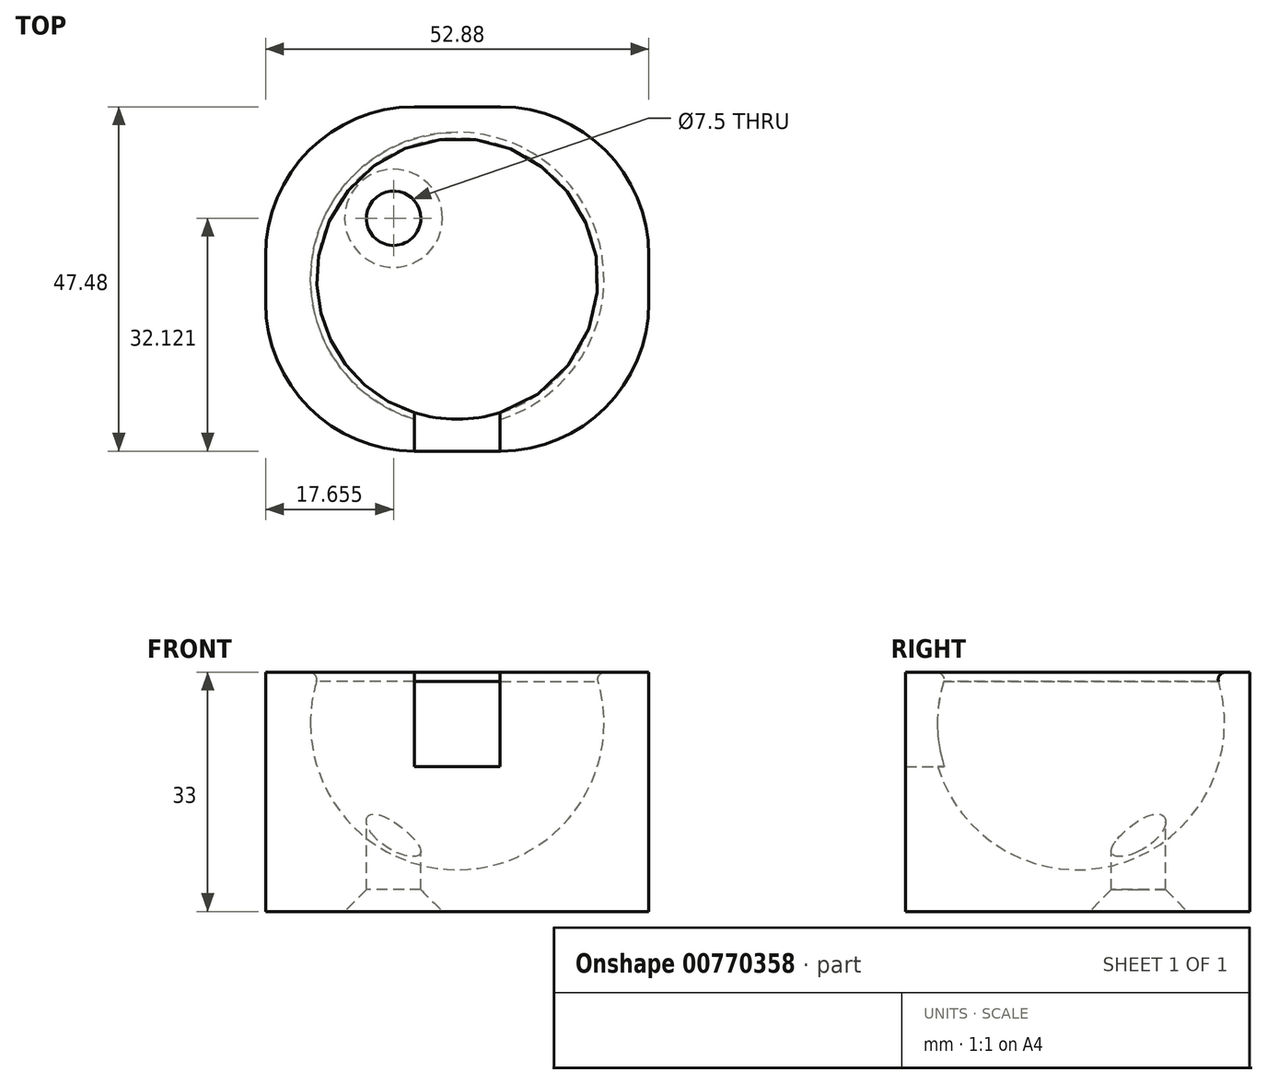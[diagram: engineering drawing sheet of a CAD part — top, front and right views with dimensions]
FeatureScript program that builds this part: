
annotation { "Feature Type Name" : "Feature", "Feature Type Description" : "" }
export const myFeature = defineFeature(function(context is Context, id is Id, definition is map)
    precondition{}
    {
        {
            var Q0;
            Q0=qCreatedBy(makeId("Top.planeOp"),FACE);
            var sketch = newSketch(context, id + "F0", { "sketchPlane" : qUnion([Q0])});
            skLineSegment(sketch, "E0", {"start": v(0, 20.25) * mm, "end": v(0, -20.25) * mm});
            skArc(sketch, "E1", {"start": v(0, 20.25) * mm, "mid": v(-20.25, 0) * mm, "end": v(0, -20.25) * mm});
            skSolve(sketch);
        }
        {
            var Q0;
            Q0=makeQuery(id+"F0.imprint","IMPRINT",FACE,{"disambiguationData":[TD([[makeQuery(id+"F0.imprint","IMPRINT",EDGE,{"derivedFrom":sQuery(id+"F0.wireOp",EDGE,"E0")}),-1.0]])]});
            var Q1;
            Q1=sQuery(id+"F0.wireOp",EDGE,"E0");
            revolve(context, id + "F1", {"surfaceOperationType" : NewSurfaceOperationType.NEW, "entities" : qUnion([Q0]), "axis" : qUnion([Q1]), "revolveType" : RevolveType.FULL});
        }
        {
            var Q0;
            Q0=qCreatedBy(makeId("Top.planeOp"),FACE);
            var sketch = newSketch(context, id + "F2", { "sketchPlane" : qUnion([Q0])});
            skLineSegment(sketch, "E2.bottom", {"start": v(26.44, -23.74) * mm, "end": v(-26.44, -23.74) * mm});
            skLineSegment(sketch, "E2.top", {"start": v(26.44, 23.74) * mm, "end": v(-26.44, 23.74) * mm});
            skLineSegment(sketch, "E2.left", {"start": v(26.44, -23.74) * mm, "end": v(26.44, 23.74) * mm});
            skLineSegment(sketch, "E2.right", {"start": v(-26.44, -23.74) * mm, "end": v(-26.44, 23.74) * mm});
            skPoint(sketch, "E2.middle", {"position": v(0, 0) * mm});
            skSolve(sketch);
        }
        {
            var Q0;
            Q0=makeQuery(id+"F2.imprint","IMPRINT",FACE,{"disambiguationData":[TD([[makeQuery(id+"F2.imprint","IMPRINT",EDGE,{"derivedFrom":sQuery(id+"F2.wireOp",EDGE,"E2.bottom")}),-1.0]])]});
            extrude(context, id + "F3", {"entities" : qUnion([Q0]), "endBound" : BoundingType.SYMMETRIC, "depth" : 52 * mm, "offsetDistance" : 25 * mm});
        }
        {
            var Q0;
            Q0=makeQuery(id+"F1.opRevolve","SWEPT_BODY",BODY,{"disambiguationData":[OSD([sQuery(id+"F0.wireOp",EDGE,"E0"),sQuery(id+"F0.wireOp",EDGE,"E1")])]});
            var Q1;
            Q1=makeQuery(id+"F3.opExtrude","SWEPT_BODY",BODY,{"disambiguationData":[OSD([sQuery(id+"F2.wireOp",EDGE,"E2.bottom"),sQuery(id+"F2.wireOp",EDGE,"E2.top"),sQuery(id+"F2.wireOp",EDGE,"E2.left"),sQuery(id+"F2.wireOp",EDGE,"E2.right")])]});
            booleanBodies(context, id + "F4", {"operationType" : BooleanOperationType.SUBTRACTION, "tools" : qUnion([Q0]), "targets" : qUnion([Q1])});
        }
        {
            var Q0;
            Q0=makeQuery(id+"F3.opExtrude","CAP_FACE",FACE,{"disambiguationData":[OSD([sQuery(id+"F2.wireOp",EDGE,"E2.bottom"),sQuery(id+"F2.wireOp",EDGE,"E2.top"),sQuery(id+"F2.wireOp",EDGE,"E2.left"),sQuery(id+"F2.wireOp",EDGE,"E2.right")])],"isStart":false});
            extrude(context, id + "F5", {"entities" : qUnion([Q0]), "operationType" : NewBodyOperationType.REMOVE, "oppositeDirection" : true, "depth" : 19 * mm, "offsetDistance" : 25 * mm});
        }
        {
            var Q0;
            Q0=qCreatedBy(makeId("Top.planeOp"),FACE);
            var sketch = newSketch(context, id + "F6", { "sketchPlane" : qUnion([Q0])});
            skCircle(sketch, "E3", {"center": v(-8.79, 8.38) * mm, "radius": 3.75 * mm});
            skSolve(sketch);
        }
        {
            var Q0;
            Q0=qCreatedBy(makeId("Top.planeOp"),FACE);
            var sketch = newSketch(context, id + "F7", { "sketchPlane" : qUnion([Q0])});
            skCircle(sketch, "E4", {"center": v(0, 0) * mm, "radius": 19.5 * mm});
            skSolve(sketch);
        }
        {
            var Q0;
            Q0=makeQuery(id+"FvmGkh30znX9Q5g_2.-3.F6.imprint","IMPRINT",FACE,{"disambiguationData":[TD([[makeQuery(id+"FvmGkh30znX9Q5g_2.-3.F6.imprint","IMPRINT",EDGE,{"derivedFrom":sQuery(id+"FvmGkh30znX9Q5g_2.-3.F6.wireOp",EDGE,"E3")}),1.0]])]});
            var Q1;
            Q1=makeQuery(id+"F6.imprint","IMPRINT",FACE,{"disambiguationData":[TD([[makeQuery(id+"F6.imprint","IMPRINT",EDGE,{"derivedFrom":sQuery(id+"F6.wireOp",EDGE,"E3")}),1.0]])]});
            var Q2;
            Q2=makeQuery(id+"FvmGkh30znX9Q5g_2.3.F6.imprint","IMPRINT",FACE,{"disambiguationData":[TD([[makeQuery(id+"FvmGkh30znX9Q5g_2.3.F6.imprint","IMPRINT",EDGE,{"derivedFrom":sQuery(id+"FvmGkh30znX9Q5g_2.3.F6.wireOp",EDGE,"E3")}),1.0]])]});
            var Q3;
            Q3=makeQuery(id+"FvmGkh30znX9Q5g_2.-2.F6.imprint","IMPRINT",FACE,{"disambiguationData":[TD([[makeQuery(id+"FvmGkh30znX9Q5g_2.-2.F6.imprint","IMPRINT",EDGE,{"derivedFrom":sQuery(id+"FvmGkh30znX9Q5g_2.-2.F6.wireOp",EDGE,"E3")}),1.0]])]});
            extrude(context, id + "F8", {"entities" : qUnion([Q0, Q1, Q2, Q3]), "operationType" : NewBodyOperationType.REMOVE, "endBound" : BoundingType.THROUGH_ALL, "oppositeDirection" : true, "depth" : 25 * mm, "offsetDistance" : 25 * mm});
        }
        {
            var Q0;
            Q0=makeQuery(id+"F3.opExtrude","SWEPT_EDGE",EDGE,{"disambiguationData":[OSD([sQuery(id+"F2.wireOp",EDGE,"E2.bottom"),sQuery(id+"F2.wireOp",EDGE,"E2.right")])]});
            var Q1;
            Q1=makeQuery(id+"F3.opExtrude","SWEPT_EDGE",EDGE,{"disambiguationData":[OSD([sQuery(id+"F2.wireOp",EDGE,"E2.bottom"),sQuery(id+"F2.wireOp",EDGE,"E2.left")])]});
            var Q2;
            Q2=makeQuery(id+"F3.opExtrude","SWEPT_EDGE",EDGE,{"disambiguationData":[OSD([sQuery(id+"F2.wireOp",EDGE,"E2.top"),sQuery(id+"F2.wireOp",EDGE,"E2.left")])]});
            var Q3;
            Q3=makeQuery(id+"F3.opExtrude","SWEPT_EDGE",EDGE,{"disambiguationData":[OSD([sQuery(id+"F2.wireOp",EDGE,"E2.top"),sQuery(id+"F2.wireOp",EDGE,"E2.right")])]});
            fillet(context, id + "F9", {"entities" : qUnion([Q0, Q1, Q2, Q3]), "radius" : 20.5 * mm, "tangentPropagation" : true, "allowEdgeOverflow" : false});
        }
        {
            var Q0;
            Q0=makeQuery(id+"F5.boolean.opBoolean","INTERSECT",EDGE,{"derivedFrom":[makeQuery(id+"F4.opBoolean","COPY",FACE,{"derivedFrom":makeQuery(id+"F1.opRevolve","SWEPT_FACE",FACE,{"disambiguationData":[OSD([sQuery(id+"F0.wireOp",EDGE,"E1")])]})}),makeQuery(id+"F5.opExtrude","CAP_FACE",FACE,{"disambiguationData":[OSD([sQuery(id+"F2.wireOp",EDGE,"E2.bottom"),sQuery(id+"F2.wireOp",EDGE,"E2.top"),sQuery(id+"F2.wireOp",EDGE,"E2.left"),sQuery(id+"F2.wireOp",EDGE,"E2.right")])],"isStart":false})]});
            fillet(context, id + "F10", {"entities" : qUnion([Q0]), "radius" : 1 * mm, "tangentPropagation" : true, "allowEdgeOverflow" : false});
        }
        {
            var Q0;
            Q0=makeQuery(id+"F8.boolean.opBoolean","INTERSECT",EDGE,{"derivedFrom":[makeQuery(id+"F3.opExtrude","CAP_FACE",FACE,{"disambiguationData":[OSD([sQuery(id+"F2.wireOp",EDGE,"E2.bottom"),sQuery(id+"F2.wireOp",EDGE,"E2.top"),sQuery(id+"F2.wireOp",EDGE,"E2.left"),sQuery(id+"F2.wireOp",EDGE,"E2.right")])],"isStart":true}),makeQuery(id+"F8.opExtrude","SWEPT_FACE",FACE,{"disambiguationData":[OSD([sQuery(id+"FvmGkh30znX9Q5g_2.3.F6.wireOp",EDGE,"E3")])]})]});
            var Q1;
            Q1=makeQuery(id+"F8.boolean.opBoolean","INTERSECT",EDGE,{"derivedFrom":[makeQuery(id+"F3.opExtrude","CAP_FACE",FACE,{"disambiguationData":[OSD([sQuery(id+"F2.wireOp",EDGE,"E2.bottom"),sQuery(id+"F2.wireOp",EDGE,"E2.top"),sQuery(id+"F2.wireOp",EDGE,"E2.left"),sQuery(id+"F2.wireOp",EDGE,"E2.right")])],"isStart":true}),makeQuery(id+"F8.opExtrude","SWEPT_FACE",FACE,{"disambiguationData":[OSD([sQuery(id+"F6.wireOp",EDGE,"E3")])]})]});
            var Q2;
            Q2=makeQuery(id+"F8.boolean.opBoolean","INTERSECT",EDGE,{"derivedFrom":[makeQuery(id+"F3.opExtrude","CAP_FACE",FACE,{"disambiguationData":[OSD([sQuery(id+"F2.wireOp",EDGE,"E2.bottom"),sQuery(id+"F2.wireOp",EDGE,"E2.top"),sQuery(id+"F2.wireOp",EDGE,"E2.left"),sQuery(id+"F2.wireOp",EDGE,"E2.right")])],"isStart":true}),makeQuery(id+"F8.opExtrude","SWEPT_FACE",FACE,{"disambiguationData":[OSD([sQuery(id+"FvmGkh30znX9Q5g_2.-3.F6.wireOp",EDGE,"E3")])]})]});
            var Q3;
            Q3=makeQuery(id+"F8.boolean.opBoolean","INTERSECT",EDGE,{"derivedFrom":[makeQuery(id+"F3.opExtrude","CAP_FACE",FACE,{"disambiguationData":[OSD([sQuery(id+"F2.wireOp",EDGE,"E2.bottom"),sQuery(id+"F2.wireOp",EDGE,"E2.top"),sQuery(id+"F2.wireOp",EDGE,"E2.left"),sQuery(id+"F2.wireOp",EDGE,"E2.right")])],"isStart":true}),makeQuery(id+"F8.opExtrude","SWEPT_FACE",FACE,{"disambiguationData":[OSD([sQuery(id+"FvmGkh30znX9Q5g_2.-2.F6.wireOp",EDGE,"E3")])]})]});
            chamfer(context, id + "F11", {"entities" : qUnion([Q0, Q1, Q2, Q3]), "width" : 3 * mm, "tangentPropagation" : true});
        }
        {
            var Q0;
            Q0=makeQuery(id+"F5.boolean.opBoolean","COPY",FACE,{"derivedFrom":makeQuery(id+"F5.opExtrude","CAP_FACE",FACE,{"disambiguationData":[OSD([sQuery(id+"F2.wireOp",EDGE,"E2.bottom"),sQuery(id+"F2.wireOp",EDGE,"E2.top"),sQuery(id+"F2.wireOp",EDGE,"E2.left"),sQuery(id+"F2.wireOp",EDGE,"E2.right")])],"isStart":false})});
            var sketch = newSketch(context, id + "F12", { "sketchPlane" : qUnion([Q0])});
            skLineSegment(sketch, "E5.bottom", {"start": v(-5.94, -23.74) * mm, "end": v(5.93, -23.74) * mm});
            skLineSegment(sketch, "E5.top", {"start": v(-5.94, -18.21) * mm, "end": v(5.93, -18.21) * mm});
            skLineSegment(sketch, "E5.left", {"start": v(-5.94, -23.74) * mm, "end": v(-5.94, -18.21) * mm});
            skLineSegment(sketch, "E5.right", {"start": v(5.93, -23.74) * mm, "end": v(5.93, -18.21) * mm});
            skSolve(sketch);
        }
        {
            var Q0;
            Q0 = qSketchRegion(id + "F12", true);
            extrude(context, id + "F13", {"entities" : qUnion([Q0]), "operationType" : NewBodyOperationType.REMOVE, "oppositeDirection" : true, "depth" : 13 * mm, "offsetDistance" : 25 * mm});
        }
    });
